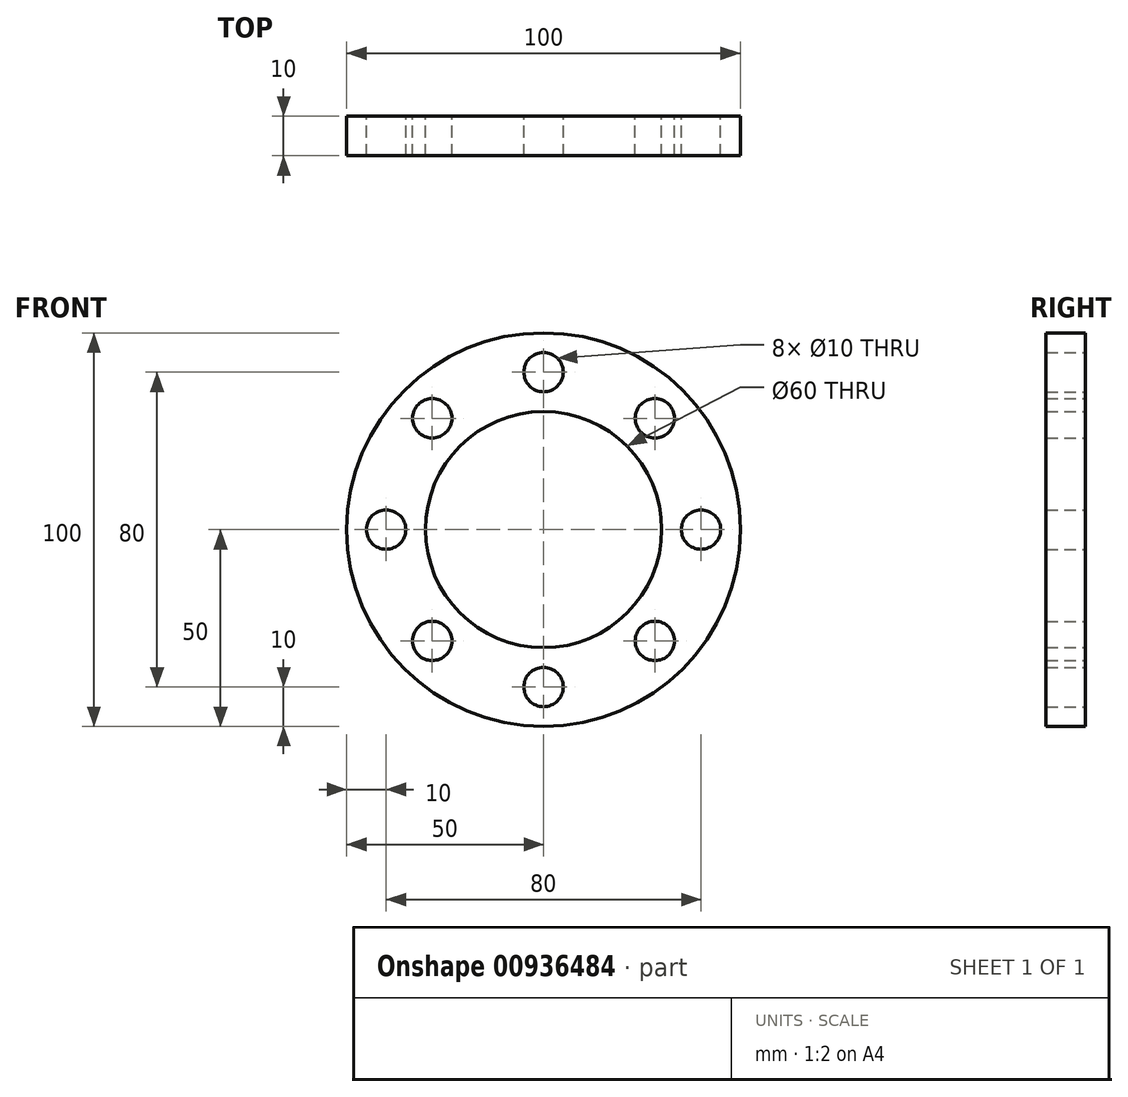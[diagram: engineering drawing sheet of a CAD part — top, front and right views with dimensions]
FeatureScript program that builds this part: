
annotation { "Feature Type Name" : "Feature", "Feature Type Description" : "" }
export const myFeature = defineFeature(function(context is Context, id is Id, definition is map)
    precondition{}
    {
        {
            var Q0;
            Q0=qCreatedBy(makeId("Front.planeOp"),FACE);
            var sketch = newSketch(context, id + "F0", { "sketchPlane" : qUnion([Q0])});
            skCircle(sketch, "E0", {"center": v(0, 0) * mm, "radius": 50 * mm});
            skCircle(sketch, "E1", {"center": v(0, 0) * mm, "radius": 30 * mm});
            skLineSegment(sketch, "E2", {"start": v(0, 0) * mm, "end": v(0, 50) * mm});
            skCircle(sketch, "E3", {"center": v(0, 40) * mm, "radius": 5 * mm});
            skCircle(sketch, "E4.1.0", {"center": v(-28.28, 28.28) * mm, "radius": 5 * mm});
            skCircle(sketch, "E4.2.0", {"center": v(-40, 0) * mm, "radius": 5 * mm});
            skCircle(sketch, "E4.3.0", {"center": v(-28.28, -28.28) * mm, "radius": 5 * mm});
            skCircle(sketch, "E4.4.0", {"center": v(0, -40) * mm, "radius": 5 * mm});
            skCircle(sketch, "E4.5.0", {"center": v(28.28, -28.28) * mm, "radius": 5 * mm});
            skCircle(sketch, "E4.6.0", {"center": v(40, 0) * mm, "radius": 5 * mm});
            skCircle(sketch, "E4.7.0", {"center": v(28.28, 28.28) * mm, "radius": 5 * mm});
            skSolve(sketch);
        }
        {
            var Q0;
            Q0=makeQuery(id+"F0.imprint","IMPRINT",FACE,{"disambiguationData":[TD([[makeQuery(id+"F0.imprint","IMPRINT",EDGE,{"derivedFrom":sQuery(id+"F0.wireOp",EDGE,"E0")}),1.0]])]});
            extrude(context, id + "F1", {"entities" : qUnion([Q0]), "depth" : 10 * mm, "offsetDistance" : 25 * mm});
        }
    });
